# Revit family: Atlas_Sound_IP-22SYSM_Ceiling_Mounted
name_source: partatom
category: Communication Devices
units: mm (PartAtom-declared; Revit-internal decimal feet)

## family parameters
Always vertical = Yes
Cut with Voids When Loaded = No
Host = Ceiling
Maintain Annotation Orientation = No
Part Type = Normal
Room Calculation Point = No
Round Connector Dimension = Use Diameter
Shared = No

## types (1)
- Atlas_Sound_IP-22SYSM_Ceiling_Mounted
    Default Elevation = 0' - 0"
    Description = POE+ indoor 2' x 2' suspended ceiling mount IP speaker with paging microphone
    Expected Lifespan (Years) = 0
    Installation-Fabrication = https://www.atlasied.com
    Maintenance Schedule (Months) = 0
    Manufacturer = Atlas Sound
    Manufacturer Fax = 602-438-8692
    Manufacturer Website = https://www.atlasied.com
    Product Data = https://www.atlasied.com
    URL = https://www.atlasied.com
    Warranty Duration (Years) = 0

## geometry (parser evidence)
native form markers: Sweep x3
no freeform markers — native parametric forms only
